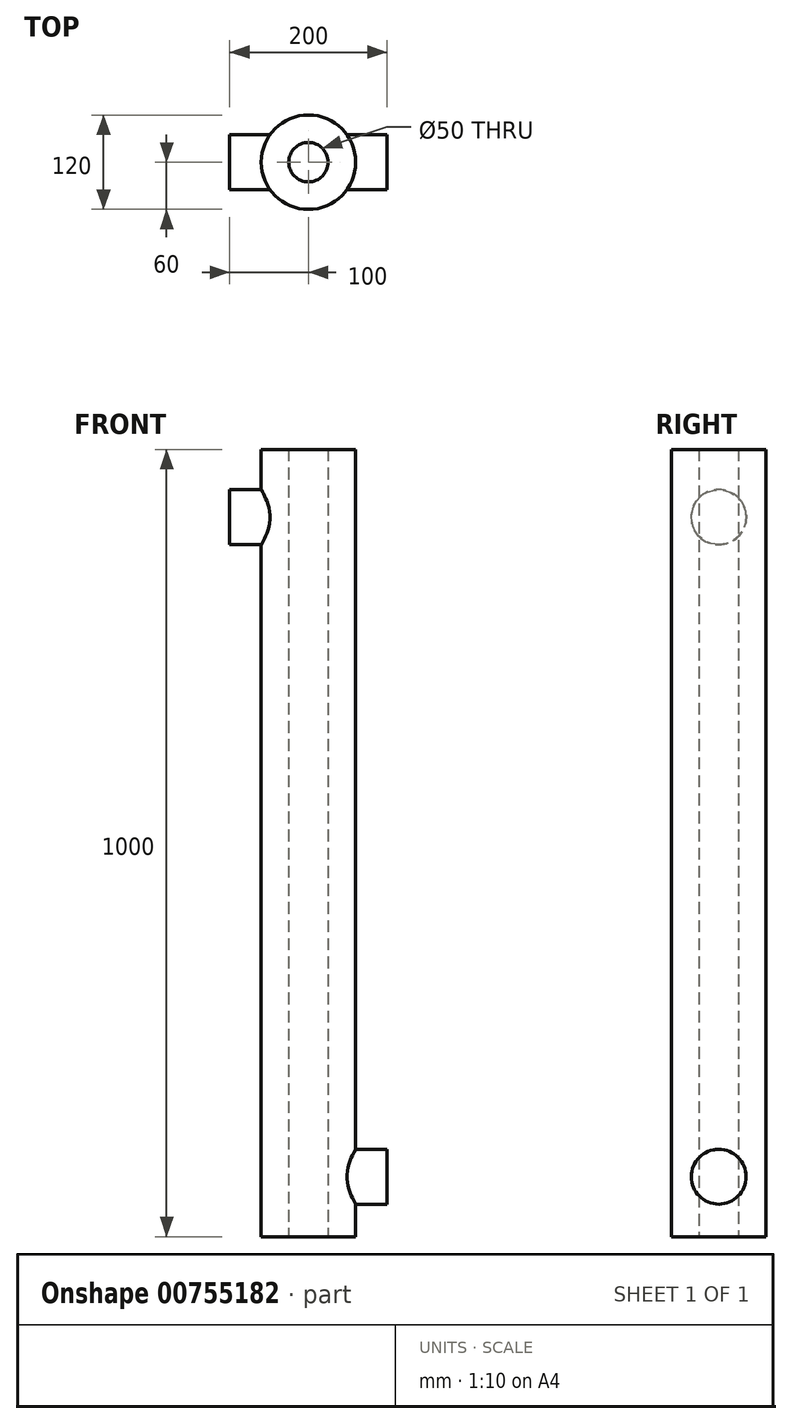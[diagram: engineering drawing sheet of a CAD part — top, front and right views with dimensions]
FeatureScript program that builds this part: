
annotation { "Feature Type Name" : "Feature", "Feature Type Description" : "" }
export const myFeature = defineFeature(function(context is Context, id is Id, definition is map)
    precondition{}
    {
        {
            var Q0;
            Q0=qCreatedBy(makeId("Top.planeOp"),FACE);
            var sketch = newSketch(context, id + "F0", { "sketchPlane" : qUnion([Q0])});
            skCircle(sketch, "E0", {"center": v(0, 0) * mm, "radius": 60 * mm});
            skCircle(sketch, "E1", {"center": v(0, 0) * mm, "radius": 25 * mm});
            skSolve(sketch);
        }
        {
            var Q0;
            Q0=makeQuery(id+"F0.imprint","IMPRINT",FACE,{"disambiguationData":[TD([[makeQuery(id+"F0.imprint","IMPRINT",EDGE,{"derivedFrom":sQuery(id+"F0.wireOp",EDGE,"E0")}),1.0]])]});
            extrude(context, id + "F1", {"entities" : qUnion([Q0]), "endBound" : BoundingType.SYMMETRIC, "depth" : 1000 * mm, "offsetDistance" : 25 * mm});
        }
        {
            var Q0;
            Q0=qCreatedBy(makeId("Right.planeOp"),FACE);
            var sketch = newSketch(context, id + "F2", { "sketchPlane" : qUnion([Q0])});
            skCircle(sketch, "E2", {"center": v(0, -423.9) * mm, "radius": 34.77 * mm});
            skSolve(sketch);
        }
        {
            var Q0;
            Q0 = qSketchRegion(id + "F2", true);
            var Q1;
            Q1=makeQuery(id+"F1.opExtrude","SWEPT_FACE",FACE,{"disambiguationData":[OSD([sQuery(id+"F0.wireOp",EDGE,"E0")])]});
            var Q2;
            Q2=qCreatedBy(makeId("Origin.pointOp"),VERTEX);
            extrude(context, id + "F3", {"entities" : qUnion([Q0]), "operationType" : NewBodyOperationType.ADD, "depth" : 100 * mm, "offsetDistance" : 25 * mm, "hasSecondDirection" : true, "secondDirectionBound" : SecondDirectionBoundingType.UP_TO_SURFACE, "secondDirectionOppositeDirection" : false, "secondDirectionDepth" : 0 * mm, "secondDirectionBoundEntityFace" : qUnion([Q1]), "secondDirectionBoundEntityVertex" : qUnion([Q2]), "hasSecondDirectionOffset" : true, "secondDirectionOffsetDistance" : 0 * mm});
        }
        {
            var Q0;
            Q0=qCreatedBy(makeId("Right.planeOp"),FACE);
            var sketch = newSketch(context, id + "F4", { "sketchPlane" : qUnion([Q0])});
            skCircle(sketch, "E3", {"center": v(0, 414.06) * mm, "radius": 35 * mm});
            skSolve(sketch);
        }
        {
            var Q0;
            Q0 = qSketchRegion(id + "F4", true);
            var Q1;
            Q1=makeQuery(id+"F1.opExtrude","SWEPT_FACE",FACE,{"disambiguationData":[OSD([sQuery(id+"F0.wireOp",EDGE,"E0")])]});
            extrude(context, id + "F5", {"entities" : qUnion([Q0]), "operationType" : NewBodyOperationType.ADD, "oppositeDirection" : true, "depth" : 100 * mm, "offsetDistance" : 25 * mm, "hasSecondDirection" : true, "secondDirectionBound" : SecondDirectionBoundingType.UP_TO_SURFACE, "secondDirectionOppositeDirection" : true, "secondDirectionDepth" : 25 * mm, "secondDirectionBoundEntityFace" : qUnion([Q1]), "hasSecondDirectionOffset" : true, "secondDirectionOffsetDistance" : 0 * mm});
        }
    });
